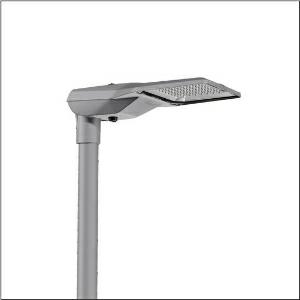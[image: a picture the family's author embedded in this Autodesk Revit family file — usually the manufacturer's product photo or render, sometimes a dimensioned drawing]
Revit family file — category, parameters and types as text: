
# Revit family: streetlight_sl_21_midi___st1_0ab_5xe3m33t08lb_f14d
name_source: partatom
category: Lighting Fixtures
units: mm (PartAtom-declared; Revit-internal decimal feet)

## family parameters
Cut with Voids When Loaded = No
Host = Face
Light Source = No
Part Type = Normal
Room Calculation Point = No
Round Connector Dimension = Use Diameter
Shared = No

## types (1)
- --- (1 x LED, 12620 lm, 99.6 W, 3000K)
    Apparent Load = 100 VA
    CIE Flux Codes = 38 73 97 100 100
    Color Rendering = 70
    Color Temperature = 3000K
    Default Elevation = 1800 mm
    Description = Streetlight SL 21 midi, mast luminaire, primary light control with lens, of PMMA, primary optical cover: cover, of toughened safety glass, transparent, light distribution: ST1.0aB, light emission: direct distribution, primary light characteristic: asymmetric, installation type: side-entry, post-top, LED, High Power LED, rated luminous flux: 12.620lm, luminous efficacy: 127lm/W, light colour: 730, colour temperature: 3000K, control gear: D4i, control: flexible luminous flux parameterisation, time-dependent luminous flux control, constant luminous flux control, overheat protection, pre-setting: logarithmic dimming characteristic, mains connection: 230..240V, AC, 50/60Hz, start of lifetime: 100W, end of service life: 102W, reduction: 46W, luminaire housing, of diecast aluminium, powder-coated, SITECO metallic grey (DB 702S), corrosivity category C5 high according to DIN EN ISO 12944, please order mast flange separately, inclination adjustable: 0°, 5°, 10°, 15°, sealing non-destructively replaceable, multi-level sealing system, length: 644mm, width: 335mm, height: 110mm, mast flange for spigot size: 42mm (side-entry): 5XC10008XM4, 60/48mm (side-entry/post-top): 5XC10108XM2, 76/60mm (side-entry/post-top): 5XC10108XM1, mounting height: 4..8m, Smart Interface below and above, protection rating (complete): IP66, insulation class (complete): insulation class II (safety insulation), certification: CE, ENEC, ENEC+, VDE, impact resistance: IK10, permissible operating ambient temperature for outdoor applications: -40..+50°C, standard-compliant lighting for roads and squares, packaging unit: 1 piece

Light Distribution: ST1.0aB
    Height = 111 mm
    Lamp = 1 x LED
    Lamp Light Flux = 12620 lm
    Lamp Power = 99.6 W
    Lamp count = 1
    Length = 644 mm
    Luminous efficacy = 127 lm/W
    Manufacturer = Siteco
    ModVariant = No
    Model = 5XE3M33T08LB
    Number of Poles = 1
    OnlyDefault = Yes
    Power Factor = 1
    Product Name = Streetlight SL 21 midi | ST1.0aB
    Product group = mast luminaire | pylon top
    ProductGroupID = 6100
    Protection Class = Protection class II
    Protection Degree = IP 66
    RLX_Detail_Level = 1
    RLX_Emergency_Light_Flux = 0 lm
    RLX_Emergency_Type = 0
    RLX_Emergency_Type_DB = No
    RlxData = <blob elided: 26985 chars, md5=4e940ecc>
    Socket = socket
    Standby Power = 0 W
    System Light Flux = 12620 lm
    System Power = 100 W
    Type Comments = factory setting: luminous flux: 100 % | dim-lin: 254 | 1020 mA
    Type Image = l_1004304.jpg
    URL = http://relux.com
    VarID = @adj_030589
    Voltage = 0 V
    Weight = 0.00 kg
    Width = 336 mm

## geometry (parser evidence)
native form markers: Blend x4, Sweep x10
no freeform markers — native parametric forms only
